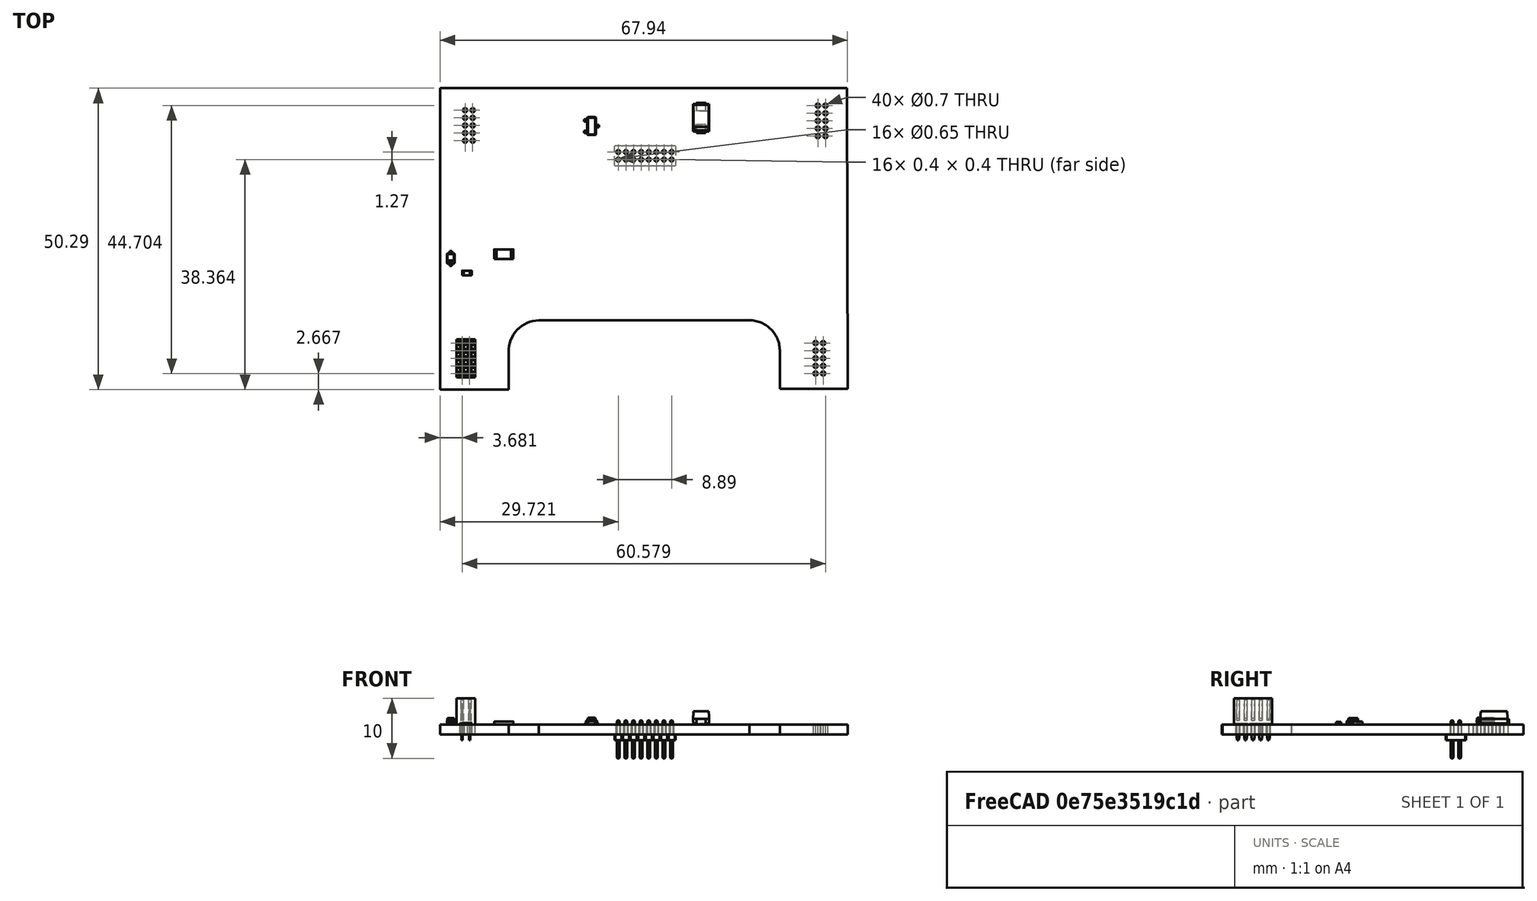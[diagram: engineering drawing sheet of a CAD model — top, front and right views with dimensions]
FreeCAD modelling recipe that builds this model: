
FCSTD DOCUMENT  (FreeCAD 1.0R39109 (Git))
Label: DIC_Addon1
License: All rights reserved
LicenseURL: http://en.wikipedia.org/wiki/All_rights_reserved
objects: App::Link×70, Part::Feature×8, App::Part×5, Sketcher::SketchObject×2, PartDesign::CoordinateSystem×1
note: 13 computed .brp shape members not serialized (recipe doc carries the construction recipe); baked Part::Feature solids carry a one-line shape summary decoded from their .brp

FEATURE [Sketcher::SketchObject] PCB_Sketch_draft
  ArcFitTolerance = 1e-06
  FullyConstrained = false
  MakeInternals = false
  sketch-geometry (10):
    g0: LineSegment StartX=11.938 StartY=-11.938 StartZ=0 EndX=11.938 EndY=-62.23 EndZ=0
    g1: LineSegment StartX=68.58 StartY=-62.103 StartZ=0 EndX=79.883 EndY=-62.103 EndZ=0
    g2: LineSegment StartX=11.938 StartY=-62.23 StartZ=0 EndX=23.3806 EndY=-62.23 EndZ=0
    g3: LineSegment StartX=23.3806 StartY=-62.23 StartZ=0 EndX=23.368 EndY=-55.9897 EndZ=0
    g4: LineSegment StartX=79.756 StartY=-11.938 StartZ=0 EndX=11.938 EndY=-11.938 EndZ=0
    g5: LineSegment StartX=68.5926 StartY=-55.8627 StartZ=0 EndX=68.58 EndY=-62.103 EndZ=0
    g6: LineSegment StartX=28.448 StartY=-50.673 StartZ=0 EndX=63.5588 EndY=-50.6595 EndZ=0
    g7: LineSegment StartX=79.883 StartY=-62.103 StartZ=0 EndX=79.756 EndY=-11.938 EndZ=0
    g8: ArcOfCircle CenterX=28.5729 CenterY=-55.8776 CenterZ=0 NormalX=0 NormalY=0 NormalZ=-1 AngleXU=-0.0215457 Radius=5.20607 StartAngle=0 EndAngle=1.56835
    g9: ArcOfCircle CenterX=63.5 CenterY=-55.753 CenterZ=0 NormalX=0 NormalY=0 NormalZ=-1 AngleXU=1.58235 Radius=5.09379 StartAngle=-4.7832e-11 EndAngle=1.58079
  constraints (10):
    c: Coincident(g0,g2)
    c: Coincident(g0,g4)
    c: Coincident(g3,g8)
    c: Coincident(g2,g3)
    c: Coincident(g6,g8)
    c: Coincident(g6,g9)
    c: Coincident(g1,g5)
    c: Coincident(g5,g9)
    c: Coincident(g4,g7)
    c: Coincident(g1,g7)
FEATURE [PartDesign::CoordinateSystem] Local_CS_25db
  AttacherType = Attacher::AttachEngine3D
  MapMode = 2
FEATURE [Part::Feature] Pcb_25db
  shape: bbox 67.95 x 50.29 x 1.6 mm, 68 faces (baked)
FEATURE [Sketcher::SketchObject] PCB_Sketch_25db
  ArcFitTolerance = 1e-06
  FullyConstrained = false
  MakeInternals = false
  sketch-geometry (10):
    g0: LineSegment StartX=11.938 StartY=-11.938 StartZ=0 EndX=11.938 EndY=-62.23 EndZ=0
    g1: LineSegment StartX=68.58 StartY=-62.103 StartZ=0 EndX=79.883 EndY=-62.103 EndZ=0
    g2: LineSegment StartX=11.938 StartY=-62.23 StartZ=0 EndX=23.3806 EndY=-62.23 EndZ=0
    g3: LineSegment StartX=23.3806 StartY=-62.23 StartZ=0 EndX=23.368 EndY=-55.9897 EndZ=0
    g4: LineSegment StartX=79.756 StartY=-11.938 StartZ=0 EndX=11.938 EndY=-11.938 EndZ=0
    g5: LineSegment StartX=68.5926 StartY=-55.8627 StartZ=0 EndX=68.58 EndY=-62.103 EndZ=0
    g6: LineSegment StartX=28.448 StartY=-50.673 StartZ=0 EndX=63.5588 EndY=-50.6595 EndZ=0
    g7: LineSegment StartX=79.883 StartY=-62.103 StartZ=0 EndX=79.756 EndY=-11.938 EndZ=0
    g8: ArcOfCircle CenterX=28.5729 CenterY=-55.8776 CenterZ=0 NormalX=0 NormalY=0 NormalZ=-1 AngleXU=-0.0215457 Radius=5.20607 StartAngle=0 EndAngle=1.56835
    g9: ArcOfCircle CenterX=63.5 CenterY=-55.753 CenterZ=0 NormalX=0 NormalY=0 NormalZ=-1 AngleXU=1.58235 Radius=5.09379 StartAngle=-4.7832e-11 EndAngle=1.58079
  constraints (10):
    c: Coincident(g0,g2)
    c: Coincident(g0,g4)
    c: Coincident(g3,g8)
    c: Coincident(g2,g3)
    c: Coincident(g6,g8)
    c: Coincident(g6,g9)
    c: Coincident(g1,g5)
    c: Coincident(g5,g9)
    c: Coincident(g4,g7)
    c: Coincident(g1,g7)
FEATURE [App::Part] Board_Geoms_25db
  Group = -> [Pcb_25db,PCB_Sketch_25db]
  Origin = -> Origin
FEATURE [Part::Feature] Shape  label="Q6_SOT_23_ffd5320711a5"
  Placement = pos=(37.211,-18.262,0) rot=(0,0,1;0rad)
  shape: bbox 2.5 x 3 x 1.2 mm, 76 faces (baked)
FEATURE [Part::Feature] Shape001  label="D16_D_SOD_323_d7651d96f6c3"
  Placement = pos=(13.7425,-40.366,0) rot=(0,0,1;1.5708rad)
  shape: bbox 1.25 x 2.5 x 1.1 mm, 67 faces (baked)
FEATURE [Part::Feature] Shape002  label="J6_PinSocket_2x05_P127mm_Vertical_83ee9fbb584e"
  Placement = pos=(16.891,-54.483,0) rot=(0,0,1;0rad)
  shape: bbox 3.05 x 6.35 x 7 mm, 320 faces (baked)
FEATURE [Part::Feature] Shape003  label="R41_R_0603_1608Metric_127fa2614279"
  Placement = pos=(16.433,-42.799,0) rot=(0,0,1;0rad)
  shape: bbox 1.6 x 0.8 x 0.45 mm, 26 faces (baked)
FEATURE [App::Link] R41_R_0603_1608Metric_127fa2614279_ln_  label="R12_R_0603_1608Metric_a0e0216bc4ce"
  LinkPlacement = pos=(30.861,-14.0945,0) rot=(0,0,1;1.5708rad)
  LinkedObject = -> Shape003
  Placement = pos=(30.861,-14.0945,0) rot=(0,0,1;1.5708rad)
FEATURE [App::Link] R41_R_0603_1608Metric_127fa2614279_ln_001  label="R13_R_0603_1608Metric_473b31106c1b"
  LinkPlacement = pos=(32.639,-18.77,0) rot=(0,0,1;1.5708rad)
  LinkedObject = -> Shape003
  Placement = pos=(32.639,-18.77,0) rot=(0,0,1;1.5708rad)
FEATURE [Part::Feature] Shape004  label="D6_D_SMA_735d77270f2b"
  Placement = pos=(55.477,-16.896,0) rot=(0,0,1;1.5708rad)
  shape: bbox 2.7 x 5 x 2.22 mm, 41 faces (baked)
FEATURE [App::Link] R41_R_0603_1608Metric_127fa2614279_ln_002  label="R9_R_0603_1608Metric_79f8a3dd54a6"
  LinkPlacement = pos=(61.214,-13.9059,0) rot=(0,0,1;3.14159rad)
  LinkedObject = -> Shape003
  Placement = pos=(61.214,-13.9059,0) rot=(0,0,1;3.14159rad)
FEATURE [App::Link] R41_R_0603_1608Metric_127fa2614279_ln_003  label="R31_R_0603_1608Metric_c49473b8d088"
  LinkPlacement = pos=(50.473,-46.8085,0) rot=(0,0,1;1.5708rad)
  LinkedObject = -> Shape003
  Placement = pos=(50.473,-46.8085,0) rot=(0,0,1;1.5708rad)
FEATURE [App::Link] R41_R_0603_1608Metric_127fa2614279_ln_004  label="R14_R_0603_1608Metric_d7197a96d642"
  LinkPlacement = pos=(37.41,-15.722,0) rot=(0,0,1;0rad)
  LinkedObject = -> Shape003
  Placement = pos=(37.41,-15.722,0) rot=(0,0,1;0rad)
FEATURE [App::Link] R41_R_0603_1608Metric_127fa2614279_ln_005  label="R35_R_0603_1608Metric_1226fcb64f1c"
  LinkPlacement = pos=(47.933,-37.9245,0) rot=(0,0,1;0rad)
  LinkedObject = -> Shape003
  Placement = pos=(47.933,-37.9245,0) rot=(0,0,1;0rad)
FEATURE [App::Link] D6_D_SMA_735d77270f2b_ln_  label="D17_D_SMA_0876cbf78d6f"
  LinkPlacement = pos=(20.828,-34.925,0) rot=(0,0,1;1.5708rad)
  LinkedObject = -> Shape004
  Placement = pos=(20.828,-34.925,0) rot=(0,0,1;1.5708rad)
FEATURE [App::Link] D6_D_SMA_735d77270f2b_ln_001  label="D15_D_SMA_1207fe425828"
  LinkPlacement = pos=(53.255,-43.21,0) rot=(0,0,1;0rad)
  LinkedObject = -> Shape004
  Placement = pos=(53.255,-43.21,0) rot=(0,0,1;0rad)
FEATURE [App::Link] D16_D_SOD_323_d7651d96f6c3_ln_  label="D13_D_SOD_323_07ad6b2cef4e"
  LinkPlacement = pos=(47.826,-32.3365,0) rot=(0,0,1;3.14159rad)
  LinkedObject = -> Shape001
  Placement = pos=(47.826,-32.3365,0) rot=(0,0,1;3.14159rad)
FEATURE [App::Link] R41_R_0603_1608Metric_127fa2614279_ln_006  label="R32_R_0603_1608Metric_48fbb2cf6ecc"
  LinkPlacement = pos=(56.061,-46.705,0) rot=(0,0,1;1.5708rad)
  LinkedObject = -> Shape003
  Placement = pos=(56.061,-46.705,0) rot=(0,0,1;1.5708rad)
FEATURE [App::Link] R41_R_0603_1608Metric_127fa2614279_ln_007  label="R24_R_0603_1608Metric_9565dda51c7b"
  LinkPlacement = pos=(50.461,-36.098,0) rot=(0,0,1;1.5708rad)
  LinkedObject = -> Shape003
  Placement = pos=(50.461,-36.098,0) rot=(0,0,1;1.5708rad)
FEATURE [App::Link] R41_R_0603_1608Metric_127fa2614279_ln_008  label="R39_R_0603_1608Metric_0d8059b3905e"
  LinkPlacement = pos=(27.857,-32.131,0) rot=(0,0,1;3.14159rad)
  LinkedObject = -> Shape003
  Placement = pos=(27.857,-32.131,0) rot=(0,0,1;3.14159rad)
FEATURE [App::Link] R41_R_0603_1608Metric_127fa2614279_ln_009  label="R11_R_0603_1608Metric_e8feb780e285"
  LinkPlacement = pos=(37.363,-14.198,0) rot=(0,0,1;0rad)
  LinkedObject = -> Shape003
  Placement = pos=(37.363,-14.198,0) rot=(0,0,1;0rad)
FEATURE [App::Link] D6_D_SMA_735d77270f2b_ln_002  label="D9_D_SMA_59bcf57c5f9f"
  LinkPlacement = pos=(51.943,-16.865,0) rot=(0,0,1;1.5708rad)
  LinkedObject = -> Shape004
  Placement = pos=(51.943,-16.865,0) rot=(0,0,1;1.5708rad)
FEATURE [App::Link] D6_D_SMA_735d77270f2b_ln_003  label="D18_D_SMA_56b2f2076145"
  LinkPlacement = pos=(24.362,-34.925,0) rot=(0,0,1;1.5708rad)
  LinkedObject = -> Shape004
  Placement = pos=(24.362,-34.925,0) rot=(0,0,1;1.5708rad)
FEATURE [App::Link] R41_R_0603_1608Metric_127fa2614279_ln_010  label="R37_R_0603_1608Metric_b9a5ae661070"
  LinkPlacement = pos=(17.25,-32.004,0) rot=(0,0,1;0rad)
  LinkedObject = -> Shape003
  Placement = pos=(17.25,-32.004,0) rot=(0,0,1;0rad)
FEATURE [App::Link] R41_R_0603_1608Metric_127fa2614279_ln_011  label="R34_R_0603_1608Metric_5b0c20e38f9c"
  LinkPlacement = pos=(44.504,-34.1145,0) rot=(0,0,1;3.14159rad)
  LinkedObject = -> Shape003
  Placement = pos=(44.504,-34.1145,0) rot=(0,0,1;3.14159rad)
FEATURE [App::Link] R41_R_0603_1608Metric_127fa2614279_ln_012  label="R33_R_0603_1608Metric_6760e7cc6251"
  LinkPlacement = pos=(44.0995,-32.3365,0) rot=(0,0,1;3.14159rad)
  LinkedObject = -> Shape003
  Placement = pos=(44.0995,-32.3365,0) rot=(0,0,1;3.14159rad)
FEATURE [App::Link] D16_D_SOD_323_d7651d96f6c3_ln_001  label="D4_D_SOD_323_fbe22daa305a"
  LinkPlacement = pos=(30.861,-18.2655,0) rot=(0,0,1;1.5708rad)
  LinkedObject = -> Shape001
  Placement = pos=(30.861,-18.2655,0) rot=(0,0,1;1.5708rad)
FEATURE [Part::Feature] Shape005  label="TH6_R_1206_3216Metric_a4174fc2a386"
  Placement = pos=(22.584,-39.624,0) rot=(0,0,1;3.14159rad)
  shape: bbox 3.2 x 1.6 x 0.55 mm, 26 faces (baked)
FEATURE [App::Link] R41_R_0603_1608Metric_127fa2614279_ln_013  label="R40_R_0603_1608Metric_99d0bb74b373"
  LinkPlacement = pos=(13.7425,-36.703,0) rot=(0,0,1;1.5708rad)
  LinkedObject = -> Shape003
  Placement = pos=(13.7425,-36.703,0) rot=(0,0,1;1.5708rad)
FEATURE [App::Link] R41_R_0603_1608Metric_127fa2614279_ln_014  label="R8_R_0603_1608Metric_f9849ceb0926"
  LinkPlacement = pos=(61.087,-19.4939,0) rot=(0,0,1;3.14159rad)
  LinkedObject = -> Shape003
  Placement = pos=(61.087,-19.4939,0) rot=(0,0,1;3.14159rad)
FEATURE [App::Link] R41_R_0603_1608Metric_127fa2614279_ln_015  label="R36_R_0603_1608Metric_b33a5e9c3cf1"
  LinkPlacement = pos=(17.377,-37.592,0) rot=(0,0,1;3.14159rad)
  LinkedObject = -> Shape003
  Placement = pos=(17.377,-37.592,0) rot=(0,0,1;3.14159rad)
FEATURE [App::Link] Q6_SOT_23_ffd5320711a5_ln_  label="Q18_SOT_23_5dae6c215293"
  LinkPlacement = pos=(16.6635,-40.259,0) rot=(0,0,1;3.14159rad)
  LinkedObject = -> Shape
  Placement = pos=(16.6635,-40.259,0) rot=(0,0,1;3.14159rad)
FEATURE [App::Link] J6_PinSocket_2x05_P127mm_Vertical_83ee9fbb584e_ln_  label="J2_PinSocket_2x05_P127mm_Vertical_fade8c78a2a7"
  LinkPlacement = pos=(76.2,-14.859,0) rot=(0,0,1;0rad)
  LinkedObject = -> Shape002
  Placement = pos=(76.2,-14.859,0) rot=(0,0,1;0rad)
FEATURE [App::Link] J6_PinSocket_2x05_P127mm_Vertical_83ee9fbb584e_ln_001  label="J5_PinSocket_2x05_P127mm_Vertical_c59673f5576a"
  LinkPlacement = pos=(16.129,-20.701,0) rot=(0,0,1;3.14159rad)
  LinkedObject = -> Shape002
  Placement = pos=(16.129,-20.701,0) rot=(0,0,1;3.14159rad)
FEATURE [App::Link] TH6_R_1206_3216Metric_a4174fc2a386_ln_  label="TH2_R_1206_3216Metric_52bc38417804"
  LinkPlacement = pos=(41.529,-18.262,0) rot=(0,0,1;1.5708rad)
  LinkedObject = -> Shape005
  Placement = pos=(41.529,-18.262,0) rot=(0,0,1;1.5708rad)
FEATURE [App::Link] D6_D_SMA_735d77270f2b_ln_004  label="D14_D_SMA_40db2f55f09c"
  LinkPlacement = pos=(53.255,-39.584,0) rot=(0,0,1;0rad)
  LinkedObject = -> Shape004
  Placement = pos=(53.255,-39.584,0) rot=(0,0,1;0rad)
FEATURE [App::Link] R41_R_0603_1608Metric_127fa2614279_ln_016  label="R42_R_0603_1608Metric_3962cb7ffa21"
  LinkPlacement = pos=(19.3305,-40.386,0) rot=(0,0,1;1.5708rad)
  LinkedObject = -> Shape003
  Placement = pos=(19.3305,-40.386,0) rot=(0,0,1;1.5708rad)
FEATURE [App::Link] J6_PinSocket_2x05_P127mm_Vertical_83ee9fbb584e_ln_002  label="J4_PinSocket_2x05_P127mm_Vertical_839abc38b667"
  LinkPlacement = pos=(75.819,-54.473,0) rot=(0,0,1;0rad)
  LinkedObject = -> Shape002
  Placement = pos=(75.819,-54.473,0) rot=(0,0,1;0rad)
FEATURE [App::Link] R41_R_0603_1608Metric_127fa2614279_ln_017  label="R10_R_0603_1608Metric_f7e09fcf0586"
  LinkPlacement = pos=(48.387,-13.563,0) rot=(0,0,1;3.14159rad)
  LinkedObject = -> Shape003
  Placement = pos=(48.387,-13.563,0) rot=(0,0,1;3.14159rad)
FEATURE [App::Link] R41_R_0603_1608Metric_127fa2614279_ln_018  label="R38_R_0603_1608Metric_5053fa264887"
  LinkPlacement = pos=(27.984,-37.719,0) rot=(0,0,1;3.14159rad)
  LinkedObject = -> Shape003
  Placement = pos=(27.984,-37.719,0) rot=(0,0,1;3.14159rad)
FEATURE [App::Link] R41_R_0603_1608Metric_127fa2614279_ln_019  label="R30_R_0603_1608Metric_0ef8a02bf31b"
  LinkPlacement = pos=(56.061,-36.0085,0) rot=(0,0,-1;1.5708rad)
  LinkedObject = -> Shape003
  Placement = pos=(56.061,-36.0085,0) rot=(0,0,-1;1.5708rad)
FEATURE [App::Link] Q6_SOT_23_ffd5320711a5_ln_001  label="Q15_SOT_23_f88ca606a138"
  LinkPlacement = pos=(47.933,-35.2575,0) rot=(0,0,1;1.5708rad)
  LinkedObject = -> Shape
  Placement = pos=(47.933,-35.2575,0) rot=(0,0,1;1.5708rad)
FEATURE [App::Link] TH6_R_1206_3216Metric_a4174fc2a386_ln_001  label="TH4_R_1206_3216Metric_6cedd577e318"
  LinkPlacement = pos=(48.568,-41.178,0) rot=(0,0,1;1.5708rad)
  LinkedObject = -> Shape005
  Placement = pos=(48.568,-41.178,0) rot=(0,0,1;1.5708rad)
FEATURE [App::Link] R41_R_0603_1608Metric_127fa2614279_ln_020  label="R5_R_0603_1608Metric_a69d22cc4bcb"
  LinkPlacement = pos=(38.6475,-31.119,0) rot=(0,0,-1;1.5708rad)
  LinkedObject = -> Shape003
  Placement = pos=(38.6475,-31.119,0) rot=(0,0,-1;1.5708rad)
FEATURE [App::Part] Top_25db
  Group = -> [Shape,Shape001,Shape002,Shape003,R41_R_0603_1608Metric_127fa2614279_ln_,R41_R_0603_1608Metric_127fa2614279_ln_001,Shape004,R41_R_0603_1608Metric_127fa2614279_ln_002,R41_R_0603_1608Metric_127fa2614279_ln_003,R41_R_0603_1608Metric_127fa2614279_ln_004,R41_R_0603_1608Metric_127fa2614279_ln_005,D6_D_SMA_735d77270f2b_ln_,D6_D_SMA_735d77270f2b_ln_001,D16_D_SOD_323_d7651d96f6c3_ln_,+27 more]
  Origin = -> Origin003
FEATURE [App::Link] R41_R_0603_1608Metric_127fa2614279_ln_021  label="R16_R_0603_1608Metric_7932c1e08af1"
  LinkPlacement = pos=(41.275,-42.313,-1.6) rot=(0.707107,0.707107,0;3.14159rad)
  LinkedObject = -> Shape003
  Placement = pos=(41.275,-42.313,-1.6) rot=(0.707107,0.707107,0;3.14159rad)
FEATURE [App::Link] R41_R_0603_1608Metric_127fa2614279_ln_022  label="R25_R_0603_1608Metric_af43064dc6b6"
  LinkPlacement = pos=(74.996,-34.8215,-1.6) rot=(0.707107,-0.707107,0;3.14159rad)
  LinkedObject = -> Shape003
  Placement = pos=(74.996,-34.8215,-1.6) rot=(0.707107,-0.707107,0;3.14159rad)
FEATURE [App::Link] R41_R_0603_1608Metric_127fa2614279_ln_023  label="R3_R_0603_1608Metric_90eb9fac611c"
  LinkPlacement = pos=(27.8525,-37.777,-1.6) rot=(0.707107,0.707107,0;3.14159rad)
  LinkedObject = -> Shape003
  Placement = pos=(27.8525,-37.777,-1.6) rot=(0.707107,0.707107,0;3.14159rad)
FEATURE [App::Link] R41_R_0603_1608Metric_127fa2614279_ln_024  label="R2_R_0603_1608Metric_a95339afed33"
  LinkPlacement = pos=(22.3534,-27.095,-1.6) rot=(0.707107,0.707107,0;3.14159rad)
  LinkedObject = -> Shape003
  Placement = pos=(22.3534,-27.095,-1.6) rot=(0.707107,0.707107,0;3.14159rad)
FEATURE [App::Link] R41_R_0603_1608Metric_127fa2614279_ln_025  label="R29_R_0603_1608Metric_a323e5d2541c"
  LinkPlacement = pos=(69.088,-31.2255,-1.6) rot=(0.707107,-0.707107,0;3.14159rad)
  LinkedObject = -> Shape003
  Placement = pos=(69.088,-31.2255,-1.6) rot=(0.707107,-0.707107,0;3.14159rad)
FEATURE [App::Link] R41_R_0603_1608Metric_127fa2614279_ln_026  label="R1_R_0603_1608Metric_b07fb1c3085f"
  LinkPlacement = pos=(27.9414,-27.222,-1.6) rot=(0.707107,0.707107,0;3.14159rad)
  LinkedObject = -> Shape003
  Placement = pos=(27.9414,-27.222,-1.6) rot=(0.707107,0.707107,0;3.14159rad)
FEATURE [App::Link] R41_R_0603_1608Metric_127fa2614279_ln_027  label="R18_R_0603_1608Metric_5d82281689e8"
  LinkPlacement = pos=(26.7885,-42.672,-1.6) rot=(0,1,0;3.14159rad)
  LinkedObject = -> Shape003
  Placement = pos=(26.7885,-42.672,-1.6) rot=(0,1,0;3.14159rad)
FEATURE [App::Link] R41_R_0603_1608Metric_127fa2614279_ln_028  label="R27_R_0603_1608Metric_214af474eae8"
  LinkPlacement = pos=(75.9085,-41.275,-1.6) rot=(1,0,0;3.14159rad)
  LinkedObject = -> Shape003
  Placement = pos=(75.9085,-41.275,-1.6) rot=(1,0,0;3.14159rad)
FEATURE [App::Link] D6_D_SMA_735d77270f2b_ln_005  label="D11_D_SMA_1ba17688d2f4"
  LinkPlacement = pos=(38.449,-38.735,-1.6) rot=(1,0,0;3.14159rad)
  LinkedObject = -> Shape004
  Placement = pos=(38.449,-38.735,-1.6) rot=(1,0,0;3.14159rad)
FEATURE [App::Link] R41_R_0603_1608Metric_127fa2614279_ln_029  label="R17_R_0603_1608Metric_89ce4ec7833c"
  LinkPlacement = pos=(26.8355,-48.26,-1.6) rot=(1,0,0;3.14159rad)
  LinkedObject = -> Shape003
  Placement = pos=(26.8355,-48.26,-1.6) rot=(1,0,0;3.14159rad)
FEATURE [App::Link] R41_R_0603_1608Metric_127fa2614279_ln_030  label="R6_R_0603_1608Metric_1afd86b5277d"
  LinkPlacement = pos=(35.7265,-28.421,-1.6) rot=(0.707107,0.707107,0;3.14159rad)
  LinkedObject = -> Shape003
  Placement = pos=(35.7265,-28.421,-1.6) rot=(0.707107,0.707107,0;3.14159rad)
FEATURE [App::Link] D16_D_SOD_323_d7651d96f6c3_ln_002  label="D10_D_SOD_323_00e277693b72"
  LinkPlacement = pos=(33.167,-46.0745,-1.6) rot=(0,1,0;3.14159rad)
  LinkedObject = -> Shape001
  Placement = pos=(33.167,-46.0745,-1.6) rot=(0,1,0;3.14159rad)
FEATURE [Part::Feature] Shape006  label="J3_PinHeader_2x08_P127mm_Vertical_13ff719d442c"
  Placement = pos=(50.551,-23.866,-1.6) rot=(0.707107,0.707107,0;3.14159rad)
  shape: bbox 10.16 x 3.4 x 6.3 mm, 340 faces (baked)
FEATURE [App::Link] D6_D_SMA_735d77270f2b_ln_006  label="D3_D_SMA_cd35c1e422c8"
  LinkPlacement = pos=(25.0905,-34.268,-1.6) rot=(0,1,0;3.14159rad)
  LinkedObject = -> Shape004
  Placement = pos=(25.0905,-34.268,-1.6) rot=(0,1,0;3.14159rad)
FEATURE [App::Link] R41_R_0603_1608Metric_127fa2614279_ln_031  label="R7_R_0603_1608Metric_afc0888e760f"
  LinkPlacement = pos=(30.6465,-28.172,-1.6) rot=(0.707107,-0.707107,0;3.14159rad)
  LinkedObject = -> Shape003
  Placement = pos=(30.6465,-28.172,-1.6) rot=(0.707107,-0.707107,0;3.14159rad)
FEATURE [App::Link] R41_R_0603_1608Metric_127fa2614279_ln_032  label="R28_R_0603_1608Metric_a4707fec901c"
  LinkPlacement = pos=(61.595,-31.0515,-1.6) rot=(0.707107,0.707107,0;3.14159rad)
  LinkedObject = -> Shape003
  Placement = pos=(61.595,-31.0515,-1.6) rot=(0.707107,0.707107,0;3.14159rad)
FEATURE [App::Link] D16_D_SOD_323_d7651d96f6c3_ln_003  label="D5_D_SOD_323_8140ef0d37c0"
  LinkPlacement = pos=(63.373,-31.095,-1.6) rot=(0.707107,0.707107,0;3.14159rad)
  LinkedObject = -> Shape001
  Placement = pos=(63.373,-31.095,-1.6) rot=(0.707107,0.707107,0;3.14159rad)
FEATURE [App::Link] D16_D_SOD_323_d7651d96f6c3_ln_004  label="D1_D_SOD_323_d5d77308ac17"
  LinkPlacement = pos=(33.1665,-31.347,-1.6) rot=(1,0,0;3.14159rad)
  LinkedObject = -> Shape001
  Placement = pos=(33.1665,-31.347,-1.6) rot=(1,0,0;3.14159rad)
FEATURE [App::Link] Q6_SOT_23_ffd5320711a5_ln_002  label="Q10_SOT_23_8cad5c28a702"
  LinkPlacement = pos=(33.147,-43.0265,-1.6) rot=(0.707107,-0.707107,0;3.14159rad)
  LinkedObject = -> Shape
  Placement = pos=(33.147,-43.0265,-1.6) rot=(0.707107,-0.707107,0;3.14159rad)
FEATURE [App::Link] R41_R_0603_1608Metric_127fa2614279_ln_033  label="R23_R_0603_1608Metric_7848ec0b3468"
  LinkPlacement = pos=(65.151,-41.529,-1.6) rot=(1,0,0;3.14159rad)
  LinkedObject = -> Shape003
  Placement = pos=(65.151,-41.529,-1.6) rot=(1,0,0;3.14159rad)
FEATURE [App::Link] TH6_R_1206_3216Metric_a4174fc2a386_ln_002  label="TH5_R_1206_3216Metric_65273da20f15"
  LinkPlacement = pos=(70.612,-34.036,-1.6) rot=(0,1,0;3.14159rad)
  LinkedObject = -> Shape005
  Placement = pos=(70.612,-34.036,-1.6) rot=(0,1,0;3.14159rad)
FEATURE [App::Link] R41_R_0603_1608Metric_127fa2614279_ln_034  label="R19_R_0603_1608Metric_b451ed5a0d5d"
  LinkPlacement = pos=(30.607,-40.6135,-1.6) rot=(0.707107,-0.707107,0;3.14159rad)
  LinkedObject = -> Shape003
  Placement = pos=(30.607,-40.6135,-1.6) rot=(0.707107,-0.707107,0;3.14159rad)
FEATURE [App::Link] R41_R_0603_1608Metric_127fa2614279_ln_035  label="R21_R_0603_1608Metric_086685fbb64e"
  LinkPlacement = pos=(64.262,-35.0285,-1.6) rot=(0.707107,0.707107,0;3.14159rad)
  LinkedObject = -> Shape003
  Placement = pos=(64.262,-35.0285,-1.6) rot=(0.707107,0.707107,0;3.14159rad)
FEATURE [App::Link] R41_R_0603_1608Metric_127fa2614279_ln_036  label="R20_R_0603_1608Metric_74876393d18b"
  LinkPlacement = pos=(37.211,-46.0745,-1.6) rot=(1,0,0;3.14159rad)
  LinkedObject = -> Shape003
  Placement = pos=(37.211,-46.0745,-1.6) rot=(1,0,0;3.14159rad)
FEATURE [App::Link] R41_R_0603_1608Metric_127fa2614279_ln_037  label="R15_R_0603_1608Metric_62f7b17bc8fc"
  LinkPlacement = pos=(35.687,-42.313,-1.6) rot=(0.707107,-0.707107,0;3.14159rad)
  LinkedObject = -> Shape003
  Placement = pos=(35.687,-42.313,-1.6) rot=(0.707107,-0.707107,0;3.14159rad)
FEATURE [App::Link] D6_D_SMA_735d77270f2b_ln_007  label="D2_D_SMA_e8f0f4ea1691"
  LinkPlacement = pos=(25.0905,-30.734,-1.6) rot=(0,1,0;3.14159rad)
  LinkedObject = -> Shape004
  Placement = pos=(25.0905,-30.734,-1.6) rot=(0,1,0;3.14159rad)
FEATURE [App::Link] TH6_R_1206_3216Metric_a4174fc2a386_ln_003  label="TH1_R_1206_3216Metric_ce9414de59a2"
  LinkPlacement = pos=(29.8845,-32.617,-1.6) rot=(0.707107,0.707107,0;3.14159rad)
  LinkedObject = -> Shape005
  Placement = pos=(29.8845,-32.617,-1.6) rot=(0.707107,0.707107,0;3.14159rad)
FEATURE [App::Link] D6_D_SMA_735d77270f2b_ln_008  label="D12_D_SMA_21d0ff51f2b2"
  LinkPlacement = pos=(38.449,-35.201,-1.6) rot=(1,0,0;3.14159rad)
  LinkedObject = -> Shape004
  Placement = pos=(38.449,-35.201,-1.6) rot=(1,0,0;3.14159rad)
FEATURE [App::Link] TH6_R_1206_3216Metric_a4174fc2a386_ln_004  label="TH3_R_1206_3216Metric_be97d367e00d"
  LinkPlacement = pos=(33.782,-36.852,-1.6) rot=(0.707107,-0.707107,0;3.14159rad)
  LinkedObject = -> Shape005
  Placement = pos=(33.782,-36.852,-1.6) rot=(0.707107,-0.707107,0;3.14159rad)
FEATURE [App::Link] D6_D_SMA_735d77270f2b_ln_009  label="D8_D_SMA_7218f854b2e2"
  LinkPlacement = pos=(72.39,-38.703,-1.6) rot=(0.707107,-0.707107,0;3.14159rad)
  LinkedObject = -> Shape004
  Placement = pos=(72.39,-38.703,-1.6) rot=(0.707107,-0.707107,0;3.14159rad)
FEATURE [App::Link] Q6_SOT_23_ffd5320711a5_ln_003  label="Q3_SOT_23_dc7f19c19d1b"
  LinkPlacement = pos=(33.1865,-28.299,-1.6) rot=(0.707107,-0.707107,0;3.14159rad)
  LinkedObject = -> Shape
  Placement = pos=(33.1865,-28.299,-1.6) rot=(0.707107,-0.707107,0;3.14159rad)
FEATURE [App::Link] R41_R_0603_1608Metric_127fa2614279_ln_038  label="R4_R_0603_1608Metric_2e89caf32d98"
  LinkPlacement = pos=(22.2645,-37.8005,-1.6) rot=(0.707107,-0.707107,0;3.14159rad)
  LinkedObject = -> Shape003
  Placement = pos=(22.2645,-37.8005,-1.6) rot=(0.707107,-0.707107,0;3.14159rad)
FEATURE [App::Link] R41_R_0603_1608Metric_127fa2614279_ln_039  label="R22_R_0603_1608Metric_94414fea2e43"
  LinkPlacement = pos=(33.1235,-40.3595,-1.6) rot=(1,0,0;3.14159rad)
  LinkedObject = -> Shape003
  Placement = pos=(33.1235,-40.3595,-1.6) rot=(1,0,0;3.14159rad)
FEATURE [App::Link] D6_D_SMA_735d77270f2b_ln_010  label="D7_D_SMA_2e44e889cb4e"
  LinkPlacement = pos=(68.834,-38.703,-1.6) rot=(0.707107,-0.707107,0;3.14159rad)
  LinkedObject = -> Shape004
  Placement = pos=(68.834,-38.703,-1.6) rot=(0.707107,-0.707107,0;3.14159rad)
FEATURE [App::Link] R41_R_0603_1608Metric_127fa2614279_ln_040  label="R26_R_0603_1608Metric_d41138b5fa4f"
  LinkPlacement = pos=(64.389,-28.281,-1.6) rot=(1,0,0;3.14159rad)
  LinkedObject = -> Shape003
  Placement = pos=(64.389,-28.281,-1.6) rot=(1,0,0;3.14159rad)
FEATURE [App::Link] Q6_SOT_23_ffd5320711a5_ln_004  label="Q12_SOT_23_6e3906f2bc9c"
  LinkPlacement = pos=(66.421,-31.202,-1.6) rot=(0,1,0;3.14159rad)
  LinkedObject = -> Shape
  Placement = pos=(66.421,-31.202,-1.6) rot=(0,1,0;3.14159rad)
FEATURE [App::Part] Bot_25db
  Group = -> [R41_R_0603_1608Metric_127fa2614279_ln_021,R41_R_0603_1608Metric_127fa2614279_ln_022,R41_R_0603_1608Metric_127fa2614279_ln_023,R41_R_0603_1608Metric_127fa2614279_ln_024,R41_R_0603_1608Metric_127fa2614279_ln_025,R41_R_0603_1608Metric_127fa2614279_ln_026,R41_R_0603_1608Metric_127fa2614279_ln_027,R41_R_0603_1608Metric_127fa2614279_ln_028,D6_D_SMA_735d77270f2b_ln_005,+27 more]
  Origin = -> Origin004
FEATURE [App::Part] Step_Models_25db
  Group = -> [Top_25db,Bot_25db]
  Origin = -> Origin002
FEATURE [App::Part] Board_25db  label="DIC_Addon"
  Group = -> [Local_CS_25db,Board_Geoms_25db,Step_Models_25db]
  Origin = -> Origin001
